AUTODESK INVENTOR PART (.ipt)
format: ipt  version: 2017 SP1 (Build 210196100, 196)  size: 127,488 bytes
history: native  units: mm
features: other x3, plane x1, sketch x1
ambient origin geometry x8: Origin, YZ Plane, XZ Plane, XY Plane, X Axis, Y Axis, Z Axis, Center Point
feature tree (5):
  plane  "Arbeitsebene6"
  sketch  "Skizze6"
  other  "<userpath>\Dropbox\Elektronik\aXe_Dashboard240XL\Gehäuse\Montiert.iam"
  other  "Montiert.iam"
  other  "GehäuseDeckel:1"
